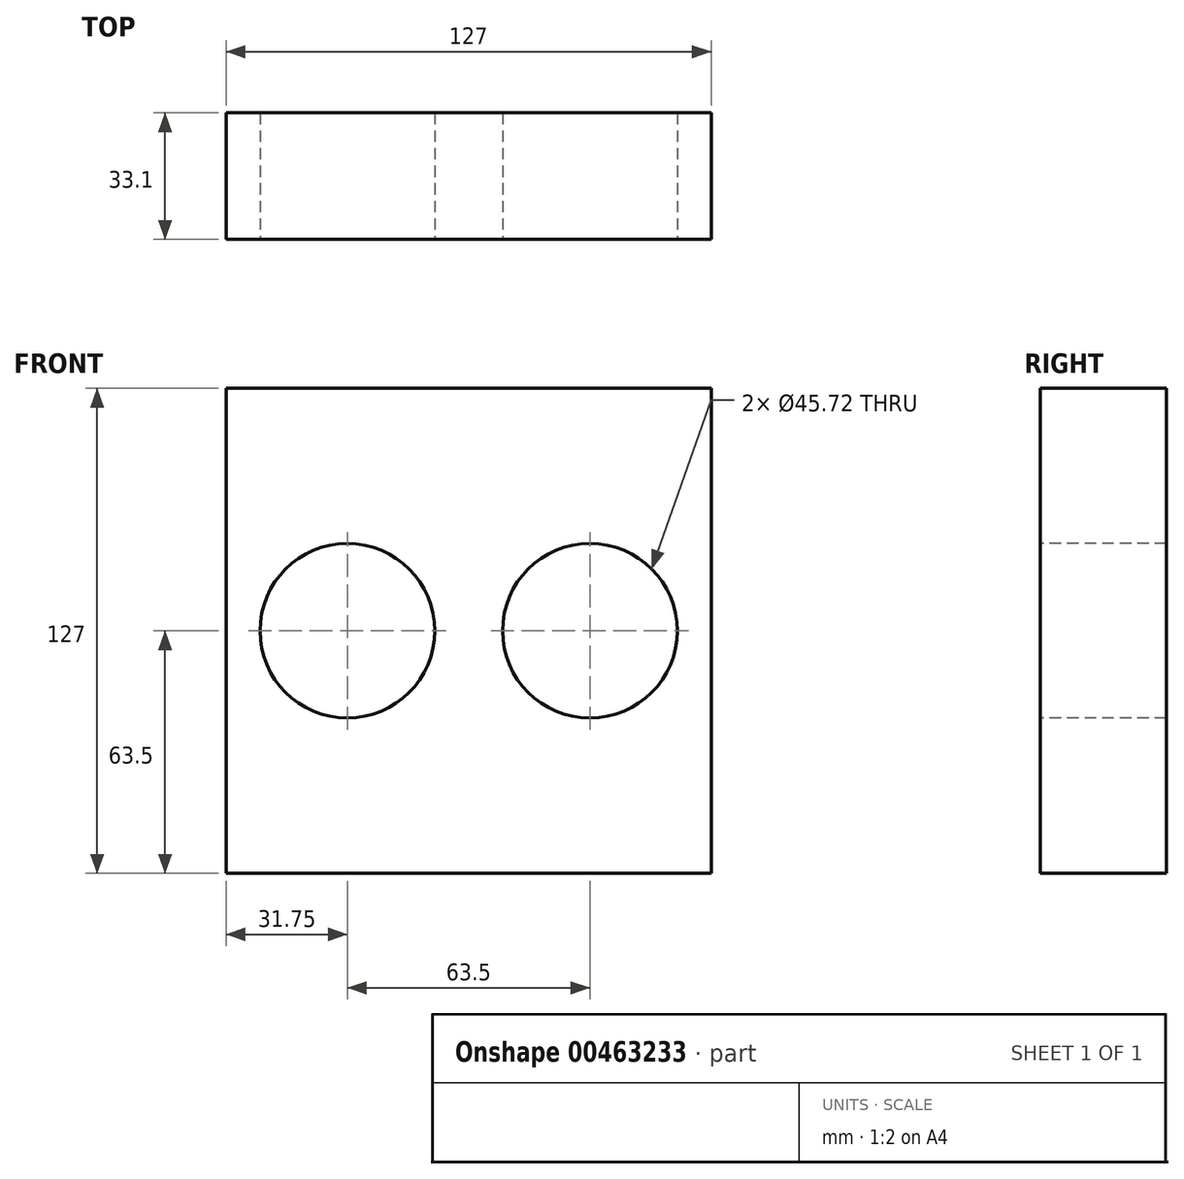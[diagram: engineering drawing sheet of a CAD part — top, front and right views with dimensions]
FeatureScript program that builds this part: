
annotation { "Feature Type Name" : "Feature", "Feature Type Description" : "" }
export const myFeature = defineFeature(function(context is Context, id is Id, definition is map)
    precondition{}
    {
        {
            var Q0;
            Q0=qCreatedBy(makeId("Front.planeOp"),FACE);
            var sketch = newSketch(context, id + "F0", { "sketchPlane" : qUnion([Q0])});
            skLineSegment(sketch, "E0.bottom", {"start": v(63.5, -63.5) * mm, "end": v(-63.5, -63.5) * mm});
            skLineSegment(sketch, "E0.top", {"start": v(63.5, 63.5) * mm, "end": v(-63.5, 63.5) * mm});
            skLineSegment(sketch, "E0.left", {"start": v(63.5, -63.5) * mm, "end": v(63.5, 63.5) * mm});
            skLineSegment(sketch, "E0.right", {"start": v(-63.5, -63.5) * mm, "end": v(-63.5, 63.5) * mm});
            skPoint(sketch, "E0.middle", {"position": v(0, 0) * mm});
            skCircle(sketch, "E1", {"center": v(-31.75, 0) * mm, "radius": 22.86 * mm});
            skCircle(sketch, "E2", {"center": v(31.75, 0) * mm, "radius": 22.86 * mm});
            skSolve(sketch);
        }
        {
            var Q0;
            Q0=makeQuery(id+"F0.imprint","IMPRINT",FACE,{"disambiguationData":[TD([[makeQuery(id+"F0.imprint","IMPRINT",EDGE,{"derivedFrom":sQuery(id+"F0.wireOp",EDGE,"E0.bottom")}),-1.0]])]});
            extrude(context, id + "F1", {"entities" : qUnion([Q0]), "oppositeDirection" : true, "depth" : 33.1 * mm});
        }
    });
